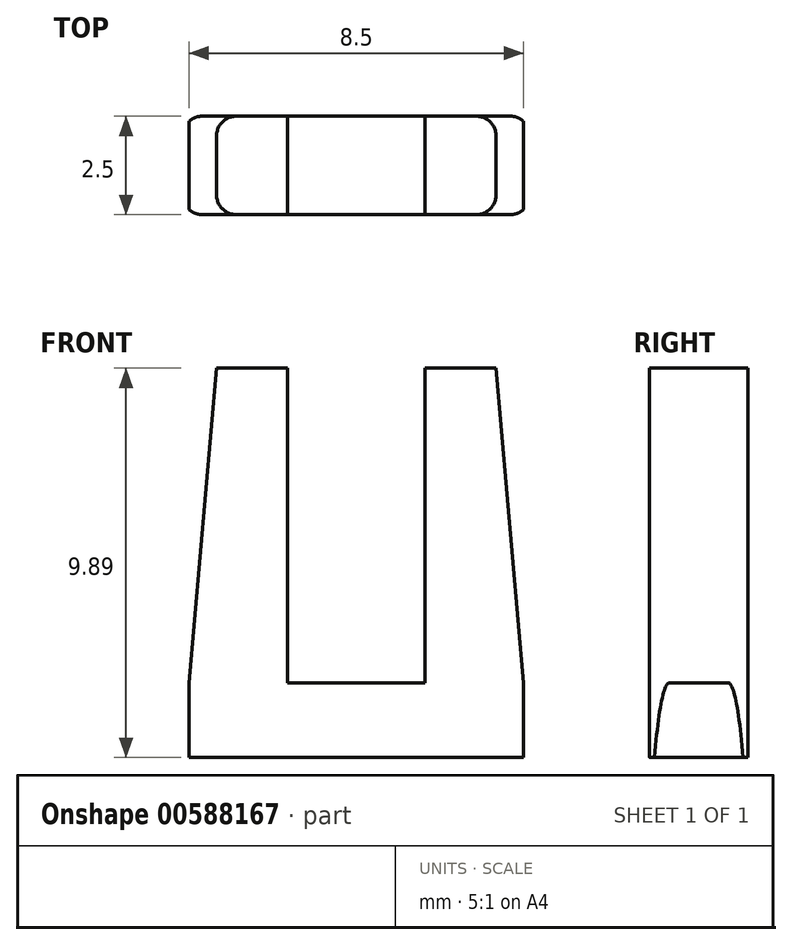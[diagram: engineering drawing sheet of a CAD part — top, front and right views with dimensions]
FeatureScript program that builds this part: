
annotation { "Feature Type Name" : "Feature", "Feature Type Description" : "" }
export const myFeature = defineFeature(function(context is Context, id is Id, definition is map)
    precondition{}
    {
        {
            var Q0;
            Q0=qCreatedBy(makeId("Front.planeOp"),FACE);
            var sketch = newSketch(context, id + "F0", { "sketchPlane" : qUnion([Q0])});
            skLineSegment(sketch, "E0", {"start": v(0, 0) * mm, "end": v(-1.75, 0) * mm});
            skLineSegment(sketch, "E1", {"start": v(-1.75, 0) * mm, "end": v(-1.75, 8) * mm});
            skLineSegment(sketch, "E2", {"start": v(-1.75, 8) * mm, "end": v(-3.55, 8) * mm});
            skLineSegment(sketch, "E3", {"start": v(0, -2.02) * mm, "end": v(0, 0) * mm});
            skLineSegment(sketch, "E4", {"start": v(-3.55, 8) * mm, "end": v(-4.25, 0) * mm});
            skLineSegment(sketch, "E5", {"start": v(-4.25, 0) * mm, "end": v(-1.75, 0) * mm});
            skPoint(sketch, "E6.start.orphan", {"position": v(-3.75, 0) * mm});
            skLineSegment(sketch, "E7.MirrorCS", {"start": v(1.75, 0) * mm, "end": v(1.75, 8) * mm});
            skLineSegment(sketch, "E8.MirrorCS", {"start": v(1.75, 8) * mm, "end": v(3.55, 8) * mm});
            skLineSegment(sketch, "E9.MirrorCS", {"start": v(3.55, 8) * mm, "end": v(4.25, 0) * mm});
            skLineSegment(sketch, "E10.MirrorCS", {"start": v(4.25, 0) * mm, "end": v(1.75, 0) * mm});
            skLineSegment(sketch, "E11", {"start": v(0, 0) * mm, "end": v(1.75, 0) * mm});
            skLineSegment(sketch, "E12", {"start": v(4.25, 0) * mm, "end": v(4.25, -1.9) * mm});
            skLineSegment(sketch, "E13", {"start": v(4.25, -1.9) * mm, "end": v(0, -1.9) * mm});
            skLineSegment(sketch, "E14", {"start": v(0, -1.9) * mm, "end": v(-4.25, -1.9) * mm});
            skLineSegment(sketch, "E15", {"start": v(-4.25, -1.9) * mm, "end": v(-4.25, 0) * mm});
            skSolve(sketch);
        }
        {
            var Q0;
            Q0 = qSketchRegion(id + "F0", true);
            extrude(context, id + "F1", {"entities" : qUnion([Q0]), "depth" : 2.5 * mm, "offsetDistance" : 25 * mm});
        }
        {
            var Q0;
            Q0=makeQuery(id+"F1.opExtrude","CAP_EDGE",EDGE,{"disambiguationData":[OSD([sQuery(id+"F0.wireOp",EDGE,"E9.MirrorCS")])],"isStart":false});
            var Q1;
            Q1=makeQuery(id+"F1.opExtrude","CAP_EDGE",EDGE,{"disambiguationData":[OSD([sQuery(id+"F0.wireOp",EDGE,"E4")])],"isStart":false});
            var Q2;
            Q2=makeQuery(id+"F1.opExtrude","CAP_EDGE",EDGE,{"disambiguationData":[OSD([sQuery(id+"F0.wireOp",EDGE,"E4")])],"isStart":true});
            var Q3;
            Q3=makeQuery(id+"F1.opExtrude","CAP_EDGE",EDGE,{"disambiguationData":[OSD([sQuery(id+"F0.wireOp",EDGE,"E9.MirrorCS")])],"isStart":true});
            fillet(context, id + "F2", {"entities" : qUnion([Q0, Q1, Q2, Q3]), "radius" : .5 * mm, "tangentPropagation" : true, "allowEdgeOverflow" : false});
        }
    });
